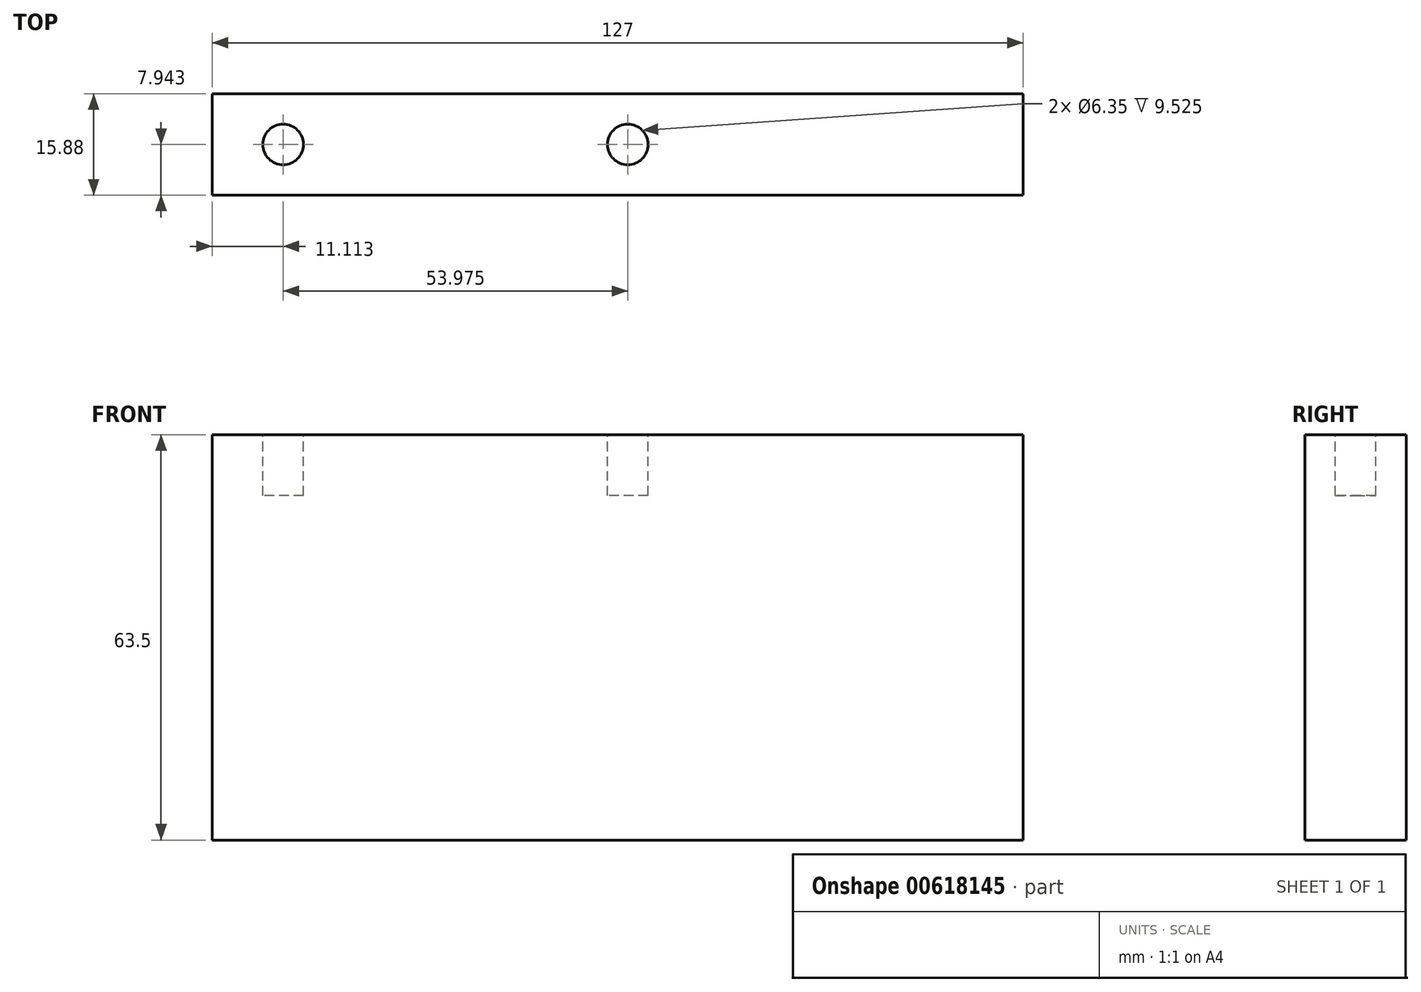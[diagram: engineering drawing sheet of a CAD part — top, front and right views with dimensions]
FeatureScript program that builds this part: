
annotation { "Feature Type Name" : "Feature", "Feature Type Description" : "" }
export const myFeature = defineFeature(function(context is Context, id is Id, definition is map)
    precondition{}
    {
        {
            var Q0;
            Q0=qCreatedBy(makeId("Front.planeOp"),FACE);
            var sketch = newSketch(context, id + "F0", { "sketchPlane" : qUnion([Q0])});
            skLineSegment(sketch, "E0.bottom", {"start": v(0, 0) * mm, "end": v(127, 0) * mm});
            skLineSegment(sketch, "E0.top", {"start": v(0, 63.5) * mm, "end": v(127, 63.5) * mm});
            skLineSegment(sketch, "E0.left", {"start": v(0, 0) * mm, "end": v(0, 63.5) * mm});
            skLineSegment(sketch, "E0.right", {"start": v(127, 0) * mm, "end": v(127, 63.5) * mm});
            skSolve(sketch);
        }
        {
            var Q0;
            Q0=qSketchRegion(id+"F0",true);
            extrude(context, id + "F1", {"entities" : qUnion([Q0]), "depth" : 15.88 * mm});
        }
        {
            var Q0;
            Q0=makeQuery(id+"F1.opExtrude","SWEPT_FACE",FACE,{"disambiguationData":[OSD([sQuery(id+"F0.wireOp",EDGE,"E0.top")])]});
            var sketch = newSketch(context, id + "F2", { "sketchPlane" : qUnion([Q0])});
            skLineSegment(sketch, "E1", {"start": v(0, -7.94) * mm, "end": v(11.11, -7.94) * mm});
            skLineSegment(sketch, "E2", {"start": v(11.11, -7.94) * mm, "end": v(65.09, -7.94) * mm});
            skLineSegment(sketch, "E3", {"start": v(65.09, -7.94) * mm, "end": v(76.2, -7.94) * mm});
            skCircle(sketch, "E4", {"center": v(11.11, -7.94) * mm, "radius": 3.18 * mm});
            skCircle(sketch, "E5", {"center": v(65.09, -7.94) * mm, "radius": 3.18 * mm});
            skSolve(sketch);
        }
        {
            var Q0;
            Q0=qSketchRegion(id+"F2",true);
            extrude(context, id + "F3", {"entities" : qUnion([Q0]), "operationType" : NewBodyOperationType.REMOVE, "oppositeDirection" : true, "depth" : 9.52 * mm});
        }
    });
